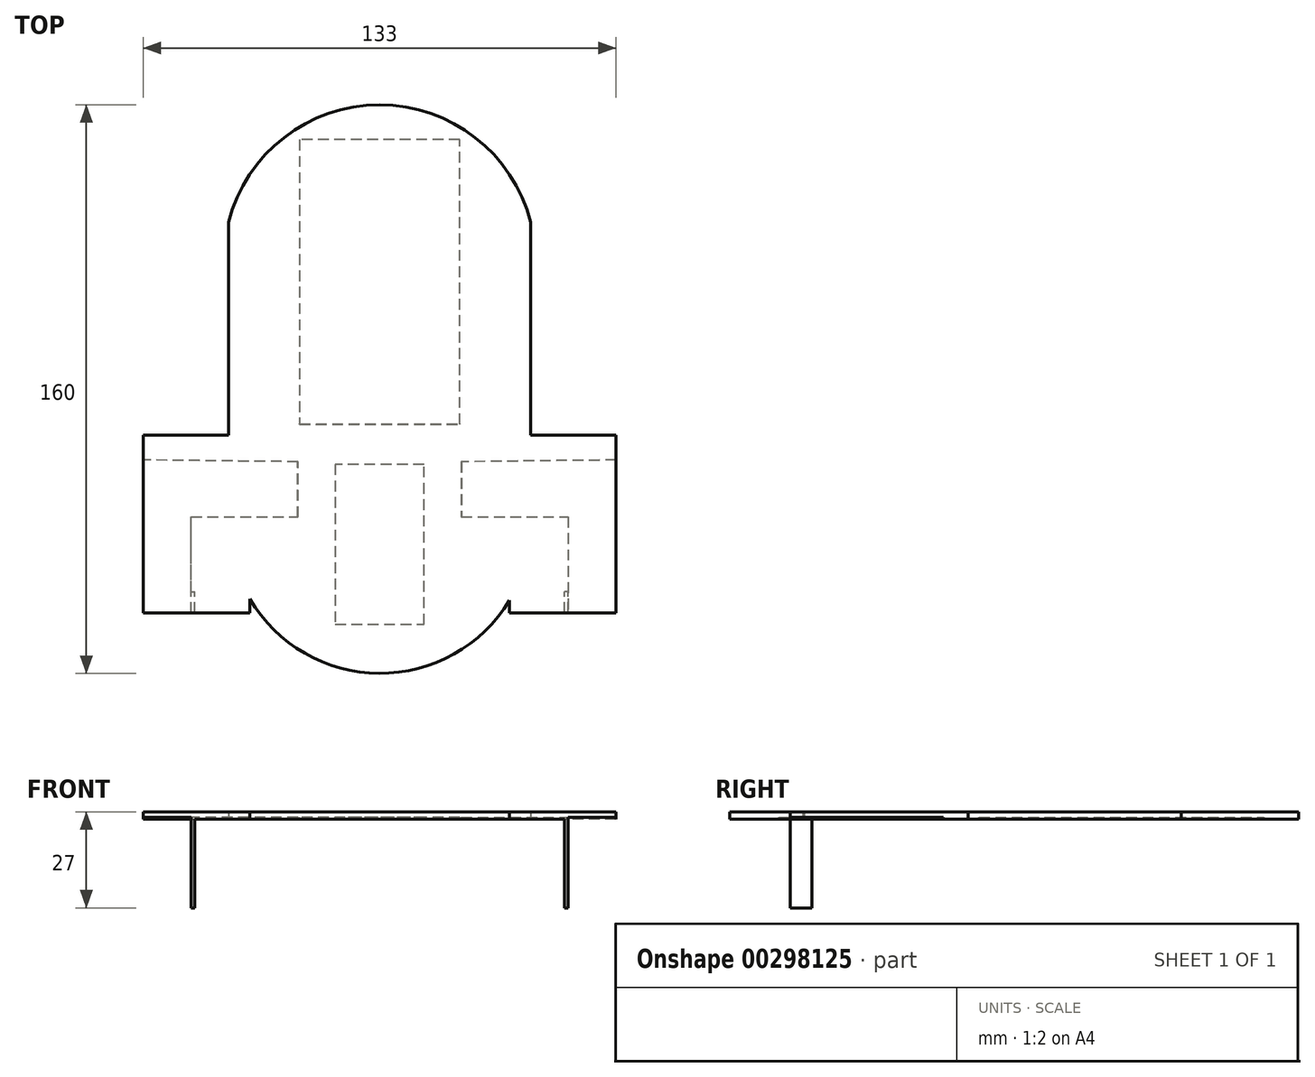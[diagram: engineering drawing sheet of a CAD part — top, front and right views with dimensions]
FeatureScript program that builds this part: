
annotation { "Feature Type Name" : "Feature", "Feature Type Description" : "" }
export const myFeature = defineFeature(function(context is Context, id is Id, definition is map)
    precondition{}
    {
        {
            var Q0;
            Q0=qCreatedBy(makeId("Top.planeOp"),FACE);
            var sketch = newSketch(context, id + "F0", { "sketchPlane" : qUnion([Q0])});
            skLineSegment(sketch, "E0.left", {"start": v(42.5, 30) * mm, "end": v(42.5, -30) * mm});
            skLineSegment(sketch, "E0.right", {"start": v(-42.5, 30) * mm, "end": v(-42.5, -30) * mm});
            skPoint(sketch, "E0.middle", {"position": v(0, 0) * mm});
            skArc(sketch, "E1", {"start": v(42.5, 30) * mm, "mid": v(0, 62.96) * mm, "end": v(-42.5, 30) * mm});
            skLineSegment(sketch, "E2.bottom", {"start": v(66.5, -30) * mm, "end": v(42.5, -30) * mm});
            skLineSegment(sketch, "E2.top", {"start": v(66.5, -80) * mm, "end": v(36.5, -80) * mm});
            skLineSegment(sketch, "E2.left", {"start": v(66.5, -30) * mm, "end": v(66.5, -80) * mm});
            skLineSegment(sketch, "E3.bottom", {"start": v(-66.5, -30) * mm, "end": v(-42.5, -30) * mm});
            skLineSegment(sketch, "E3.top", {"start": v(-66.5, -80) * mm, "end": v(-36.5, -80) * mm});
            skLineSegment(sketch, "E3.left", {"start": v(-66.5, -30) * mm, "end": v(-66.5, -80) * mm});
            skPoint(sketch, "E4.endSnap0", {"position": v(0, -30) * mm});
            skPoint(sketch, "E5.second.point", {"position": v(0, -12.04) * mm});
            skPoint(sketch, "E5.third.point", {"position": v(-39.19, -70.68) * mm});
            skArc(sketch, "E6.trimOffspring", {"start": v(-36.5, -76.09) * mm, "mid": v(-0.12, -97.04) * mm, "end": v(36.5, -76.52) * mm});
            skLineSegment(sketch, "E7.trimOffspring", {"start": v(-36.5, -76.09) * mm, "end": v(-36.5, -80) * mm});
            skLineSegment(sketch, "E8.trimOffspring", {"start": v(36.5, -76.52) * mm, "end": v(36.5, -80) * mm});
            skSolve(sketch);
        }
        {
            var Q0;
            Q0=makeQuery(id+"F0.imprint","IMPRINT",FACE,{"disambiguationData":[TD([[makeQuery(id+"F0.imprint","IMPRINT",EDGE,{"derivedFrom":sQuery(id+"F0.wireOp",EDGE,"E0.left")}),-1.0]])]});
            extrude(context, id + "F1", {"entities" : qUnion([Q0]), "depth" : 3 * mm});
        }
        {
            var Q0;
            Q0=qCreatedBy(makeId("Top.planeOp"),FACE);
            var sketch = newSketch(context, id + "F2", { "sketchPlane" : qUnion([Q0])});
            skLineSegment(sketch, "E9.bottom", {"start": v(22.5, 53.13) * mm, "end": v(-22.5, 53.13) * mm});
            skLineSegment(sketch, "E9.top", {"start": v(22.5, -26.87) * mm, "end": v(-22.5, -26.87) * mm});
            skLineSegment(sketch, "E9.left", {"start": v(22.5, 53.13) * mm, "end": v(22.5, -26.87) * mm});
            skLineSegment(sketch, "E9.right", {"start": v(-22.5, 53.13) * mm, "end": v(-22.5, -26.87) * mm});
            skPoint(sketch, "E9.middle", {"position": v(0, 13.13) * mm});
            skLineSegment(sketch, "E10.bottom", {"start": v(12.5, -38.23) * mm, "end": v(-12.5, -38.23) * mm});
            skLineSegment(sketch, "E10.top", {"start": v(12.5, -83.23) * mm, "end": v(-12.5, -83.23) * mm});
            skLineSegment(sketch, "E10.left", {"start": v(12.5, -38.23) * mm, "end": v(12.5, -83.23) * mm});
            skLineSegment(sketch, "E10.right", {"start": v(-12.5, -38.23) * mm, "end": v(-12.5, -83.23) * mm});
            skPoint(sketch, "E10.middle", {"position": v(0, -60.73) * mm});
            skSolve(sketch);
        }
        {
            var Q0;
            Q0=makeQuery(id+"F1.opExtrude","CAP_FACE",FACE,{"disambiguationData":[OSD([sQuery(id+"F0.wireOp",EDGE,"E0.left"),sQuery(id+"F0.wireOp",EDGE,"E0.right"),sQuery(id+"F0.wireOp",EDGE,"E1"),sQuery(id+"F0.wireOp",EDGE,"E2.top"),sQuery(id+"F0.wireOp",EDGE,"E2.left"),sQuery(id+"F0.wireOp",EDGE,"E2.bottom"),sQuery(id+"F0.wireOp",EDGE,"E3.top"),sQuery(id+"F0.wireOp",EDGE,"E3.left"),sQuery(id+"F0.wireOp",EDGE,"E3.bottom"),sQuery(id+"F0.wireOp",EDGE,"E6.trimOffspring"),sQuery(id+"F0.wireOp",EDGE,"E7.trimOffspring"),sQuery(id+"F0.wireOp",EDGE,"E8.trimOffspring")])],"isStart":false});
            var Q1;
            Q1 = qSketchRegion(id + "F2", true);
            extrude(context, id + "F3", {"entities" : qUnion([Q0, Q1]), "operationType" : NewBodyOperationType.REMOVE, "endBound" : BoundingType.SYMMETRIC, "oppositeDirection" : true, "depth" : 1 * mm, "hasDraft" : true, "draftAngle" : 3 * degree});
        }
        {
            var Q0;
            Q0=qCreatedBy(makeId("Top.planeOp"),FACE);
            var sketch = newSketch(context, id + "F4", { "sketchPlane" : qUnion([Q0])});
            skLineSegment(sketch, "E11.top", {"start": v(66.5, -80) * mm, "end": v(53, -80) * mm});
            skLineSegment(sketch, "E11.left", {"start": v(66.5, -37) * mm, "end": v(66.5, -80) * mm});
            skLineSegment(sketch, "E11.right", {"start": v(53, -53) * mm, "end": v(53, -80) * mm});
            skPoint(sketch, "E11.middle", {"position": v(59.75, -58.5) * mm});
            skLineSegment(sketch, "E12.top", {"start": v(-53, -80) * mm, "end": v(-66.5, -80) * mm});
            skLineSegment(sketch, "E12.left", {"start": v(-53, -53) * mm, "end": v(-53, -80) * mm});
            skLineSegment(sketch, "E12.right", {"start": v(-66.5, -37) * mm, "end": v(-66.5, -80) * mm});
            skPoint(sketch, "E12.middle", {"position": v(-59.75, -58.5) * mm});
            skLineSegment(sketch, "E13.top", {"start": v(53, -53) * mm, "end": v(23, -53) * mm});
            skLineSegment(sketch, "E13.left", {"start": v(66.5, -37) * mm, "end": v(66.5, -53) * mm});
            skLineSegment(sketch, "E13.right", {"start": v(23, -37.5) * mm, "end": v(23, -53) * mm});
            skLineSegment(sketch, "E14.top", {"start": v(-53, -53) * mm, "end": v(-23, -53) * mm});
            skLineSegment(sketch, "E14.left", {"start": v(-66.5, -37) * mm, "end": v(-66.5, -53) * mm});
            skLineSegment(sketch, "E14.right", {"start": v(-23, -37.5) * mm, "end": v(-23, -53) * mm});
            skPoint(sketch, "E14.bottom.start.orphan", {"position": v(-53, -37) * mm});
            skLineSegment(sketch, "E15", {"start": v(-66.5, -37) * mm, "end": v(-23, -37.5) * mm});
            skPoint(sketch, "E11.bottom.end.orphan", {"position": v(53, -37) * mm});
            skLineSegment(sketch, "E16", {"start": v(23, -37.5) * mm, "end": v(66.5, -37) * mm});
            skSolve(sketch);
        }
        {
            var Q0;
            Q0=makeQuery(id+"F3.boolean.opBoolean","COPY",FACE,{"derivedFrom":makeQuery(id+"F3.opExtrude","CAP_FACE",FACE,{"disambiguationData":[OSD([sQuery(id+"F0.wireOp",EDGE,"E0.left"),sQuery(id+"F0.wireOp",EDGE,"E0.right"),sQuery(id+"F0.wireOp",EDGE,"E1"),sQuery(id+"F0.wireOp",EDGE,"E2.top"),sQuery(id+"F0.wireOp",EDGE,"E2.left"),sQuery(id+"F0.wireOp",EDGE,"E2.bottom"),sQuery(id+"F0.wireOp",EDGE,"E3.top"),sQuery(id+"F0.wireOp",EDGE,"E3.left"),sQuery(id+"F0.wireOp",EDGE,"E3.bottom"),sQuery(id+"F0.wireOp",EDGE,"E6.trimOffspring"),sQuery(id+"F0.wireOp",EDGE,"E7.trimOffspring"),sQuery(id+"F0.wireOp",EDGE,"E8.trimOffspring")])],"isStart":false})});
            var Q1;
            Q1 = qSketchRegion(id + "F4", true);
            extrude(context, id + "F5", {"entities" : qUnion([Q0, Q1]), "operationType" : NewBodyOperationType.REMOVE, "endBound" : BoundingType.SYMMETRIC, "oppositeDirection" : true, "depth" : 1 * mm, "hasDraft" : true, "draftAngle" : 3 * degree, "hasSecondDirection" : true, "secondDirectionOppositeDirection" : false, "secondDirectionDepth" : 25 * mm});
        }
        {
            var Q0;
            Q0=qCreatedBy(makeId("Top.planeOp"),FACE);
            var sketch = newSketch(context, id + "F6", { "sketchPlane" : qUnion([Q0])});
            skLineSegment(sketch, "E17.bottom", {"start": v(-53, -80) * mm, "end": v(-52, -80) * mm});
            skLineSegment(sketch, "E17.top", {"start": v(-53, -74) * mm, "end": v(-52, -74) * mm});
            skLineSegment(sketch, "E17.left", {"start": v(-53, -80) * mm, "end": v(-53, -74) * mm});
            skLineSegment(sketch, "E17.right", {"start": v(-52, -80) * mm, "end": v(-52, -74) * mm});
            skLineSegment(sketch, "E18.bottom", {"start": v(53, -80) * mm, "end": v(52, -80) * mm});
            skLineSegment(sketch, "E18.top", {"start": v(53, -74) * mm, "end": v(52, -74) * mm});
            skLineSegment(sketch, "E18.left", {"start": v(53, -80) * mm, "end": v(53, -74) * mm});
            skLineSegment(sketch, "E18.right", {"start": v(52, -80) * mm, "end": v(52, -74) * mm});
            skSolve(sketch);
        }
        {
            var Q0;
            Q0 = qSketchRegion(id + "F6", true);
            extrude(context, id + "F7", {"entities" : qUnion([Q0]), "operationType" : NewBodyOperationType.ADD, "oppositeDirection" : true, "depth" : 25 * mm});
        }
    });
